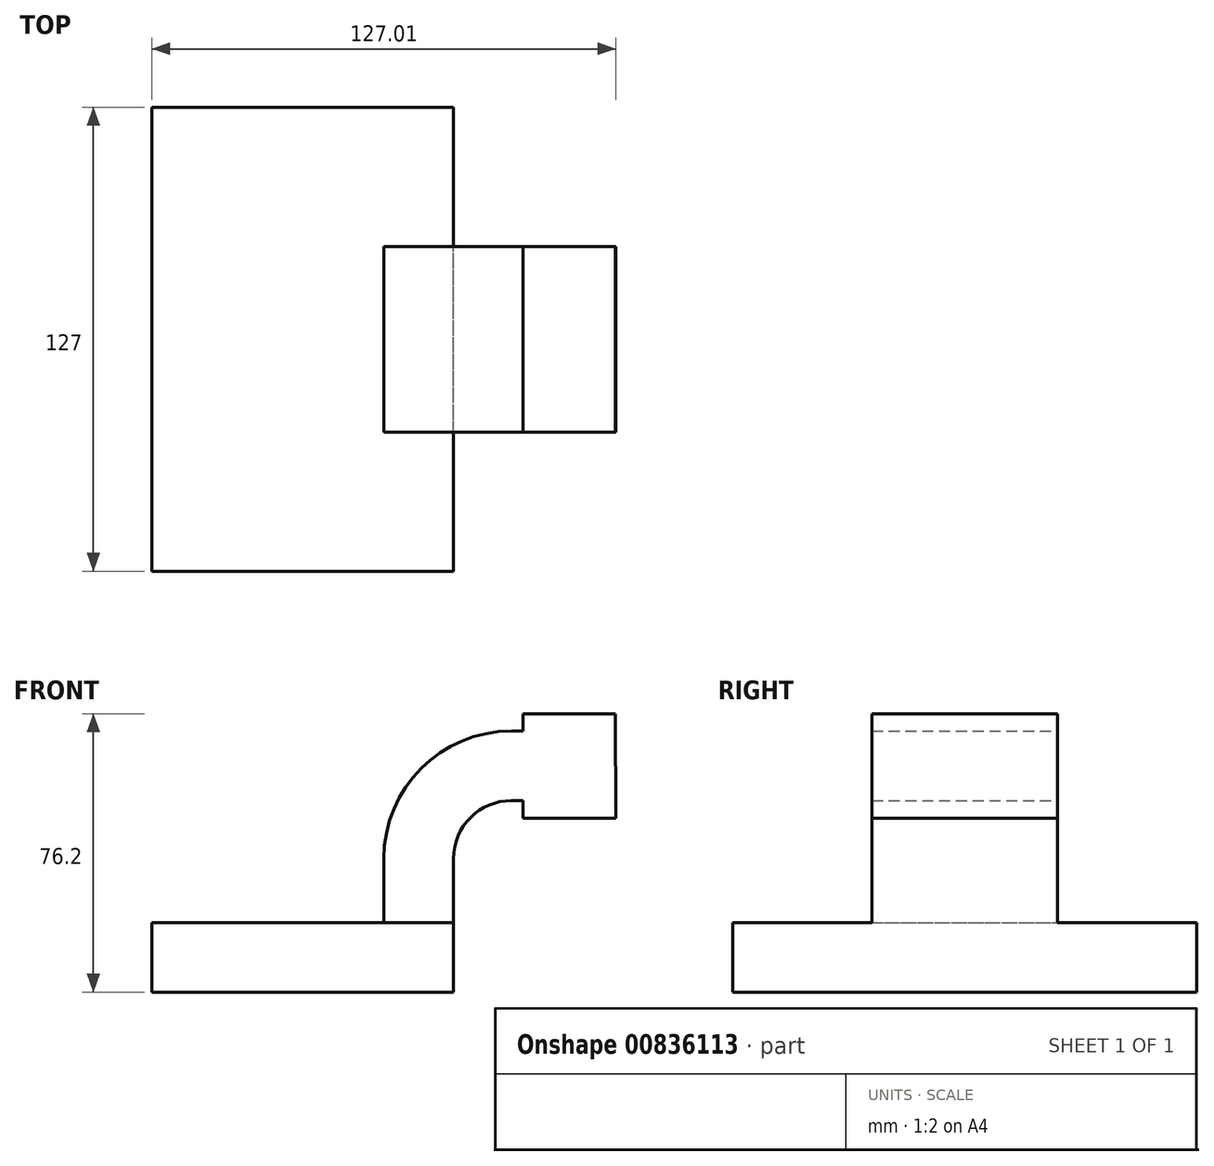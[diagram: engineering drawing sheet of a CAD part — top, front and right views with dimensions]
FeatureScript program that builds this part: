
annotation { "Feature Type Name" : "Feature", "Feature Type Description" : "" }
export const myFeature = defineFeature(function(context is Context, id is Id, definition is map)
    precondition{}
    {
        {
            var Q0;
            Q0=qCreatedBy(makeId("Front.planeOp"),FACE);
            var sketch = newSketch(context, id + "F0", { "sketchPlane" : qUnion([Q0])});
            skLineSegment(sketch, "E0.bottom", {"start": v(41.27, 9.53) * mm, "end": v(-41.28, 9.53) * mm});
            skLineSegment(sketch, "E0.top", {"start": v(41.28, -9.52) * mm, "end": v(-41.27, -9.52) * mm});
            skLineSegment(sketch, "E0.left", {"start": v(41.28, 9.53) * mm, "end": v(41.28, -9.52) * mm});
            skLineSegment(sketch, "E0.right", {"start": v(-41.28, 9.53) * mm, "end": v(-41.27, -9.52) * mm});
            skPoint(sketch, "E0.middle", {"position": v(0, 0) * mm});
            skLineSegment(sketch, "E1", {"start": v(41.27, 9.53) * mm, "end": v(41.27, 27) * mm});
            skArc(sketch, "E2", {"start": v(41.27, 27) * mm, "mid": v(45.92, 38.23) * mm, "end": v(57.15, 42.88) * mm});
            skLineSegment(sketch, "E3.bottom", {"start": v(111.12, 66.68) * mm, "end": v(60.32, 66.68) * mm});
            skLineSegment(sketch, "E3.top", {"start": v(111.12, 38.1) * mm, "end": v(60.33, 38.1) * mm});
            skLineSegment(sketch, "E3.left", {"start": v(111.12, 66.68) * mm, "end": v(111.12, 38.1) * mm});
            skLineSegment(sketch, "E3.right", {"start": v(60.32, 66.68) * mm, "end": v(60.33, 38.1) * mm});
            skPoint(sketch, "E3.middle", {"position": v(85.72, 52.39) * mm});
            skLineSegment(sketch, "E4", {"start": v(57.15, 42.88) * mm, "end": v(85.55, 42.88) * mm});
            skLineSegment(sketch, "E5.0", {"start": v(57.15, 61.93) * mm, "end": v(85.55, 61.93) * mm});
            skArc(sketch, "E5.1", {"start": v(22.23, 27) * mm, "mid": v(32.45, 51.7) * mm, "end": v(57.15, 61.93) * mm});
            skLineSegment(sketch, "E5.2", {"start": v(22.22, 9.53) * mm, "end": v(22.22, 27) * mm});
            skLineSegment(sketch, "E6", {"start": v(85.72, 38.1) * mm, "end": v(85.55, 66.68) * mm});
            skFitSpline(sketch, "E7", {"points": [v(-41.28, 9.52) * mm, v(57.15, 61.93) * mm], "startDerivative": vector(11.84, 35.97) * mm, "endDerivative": vector(210.88, -1.7) * mm});
            skSolve(sketch);
        }
        {
            var Q0;
            Q0=makeQuery(id+"F0.imprint","IMPRINT",FACE,{"disambiguationData":[TD([[makeQuery(id+"F0.imprint","IMPRINT",EDGE,{"derivedFrom":sQuery(id+"F0.wireOp",EDGE,"E0.top")}),-1.0]])]});
            extrude(context, id + "F1", {"entities" : qUnion([Q0]), "endBound" : BoundingType.SYMMETRIC, "depth" : 127 * mm, "offsetDistance" : 25.4 * mm});
        }
        {
            var Q0;
            {var subQ6=sQuery(id+"F0.wireOp",EDGE,"E6");Q0=makeQuery(id+"F0.imprint","IMPRINT",FACE,{"disambiguationData":[TD([[makeQuery(id+"F0.imprint","IMPRINT",EDGE,{"derivedFrom":subQ6}),1.0]])]});}
            var Q1;
            {var subQ7=sQuery(id+"F0.wireOp",EDGE,"E1");Q1=makeQuery(id+"F0.imprint","IMPRINT",FACE,{"disambiguationData":[TD([[makeQuery(id+"F0.imprint","IMPRINT",EDGE,{"derivedFrom":subQ7}),1.0]])]});}
            extrude(context, id + "F2", {"entities" : qUnion([Q0, Q1]), "operationType" : NewBodyOperationType.ADD, "endBound" : BoundingType.SYMMETRIC, "depth" : 50.8 * mm, "offsetDistance" : 25.4 * mm});
        }
    });
